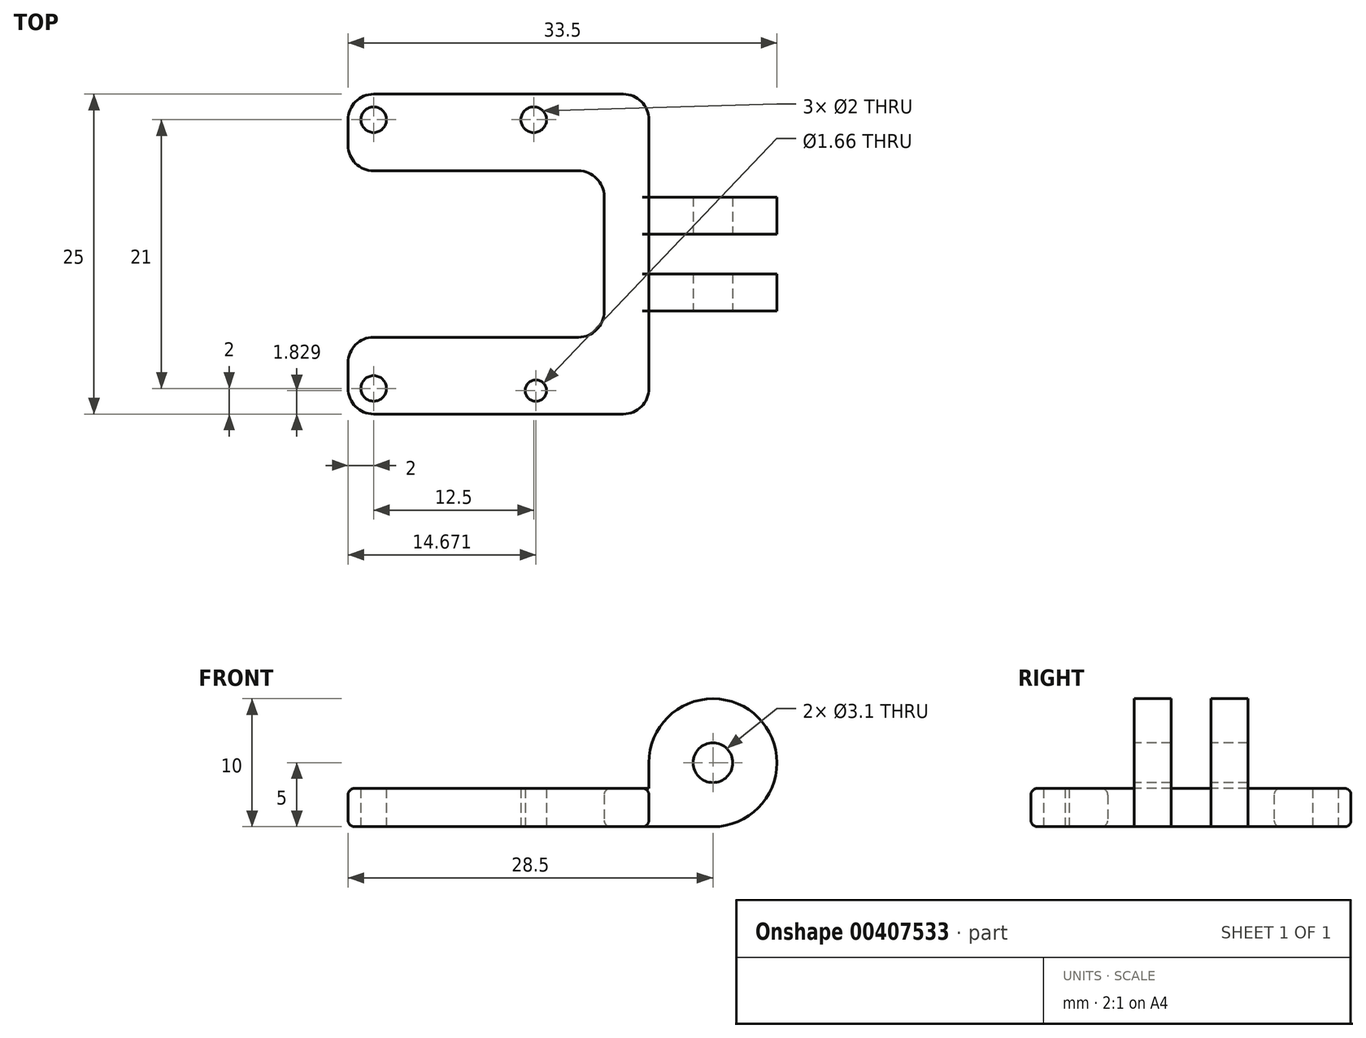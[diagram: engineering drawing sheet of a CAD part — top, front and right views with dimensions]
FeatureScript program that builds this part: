
annotation { "Feature Type Name" : "Feature", "Feature Type Description" : "" }
export const myFeature = defineFeature(function(context is Context, id is Id, definition is map)
    precondition{}
    {
        {
            var Q0;
            Q0=qCreatedBy(makeId("Top.planeOp"),FACE);
            var sketch = newSketch(context, id + "F0", { "sketchPlane" : qUnion([Q0])});
            skLineSegment(sketch, "E0.bottom", {"start": v(9.75, 12.5) * mm, "end": v(-9.75, 12.5) * mm});
            skLineSegment(sketch, "E0.top", {"start": v(9.75, -12.5) * mm, "end": v(-9.75, -12.5) * mm});
            skLineSegment(sketch, "E0.left", {"start": v(11.75, 10.5) * mm, "end": v(11.75, -1.55) * mm});
            skLineSegment(sketch, "E0.right", {"start": v(-11.75, 10.5) * mm, "end": v(-11.75, 8.5) * mm});
            skCircle(sketch, "E1", {"center": v(-9.75, -10.5) * mm, "radius": 1 * mm});
            skCircle(sketch, "E2", {"center": v(-9.75, 10.5) * mm, "radius": 1 * mm});
            skCircle(sketch, "E3", {"center": v(2.75, 10.5) * mm, "radius": 1 * mm});
            skCircle(sketch, "E4", {"center": v(2.92, -10.67) * mm, "radius": 0.83 * mm});
            skLineSegment(sketch, "E5.bottom", {"start": v(-9.75, 6.5) * mm, "end": v(6.25, 6.5) * mm});
            skLineSegment(sketch, "E5.top", {"start": v(-9.75, -6.5) * mm, "end": v(6.25, -6.5) * mm});
            skLineSegment(sketch, "E5.left", {"start": v(-11.75, 6.5) * mm, "end": v(-11.75, 6.5) * mm});
            skLineSegment(sketch, "E5.right", {"start": v(8.25, 4.5) * mm, "end": v(8.25, -4.5) * mm});
            skLineSegment(sketch, "E6", {"start": v(0, 0) * mm, "end": v(28.53, 0) * mm, "construction": true});
            skLineSegment(sketch, "E7", {"start": v(-11.75, -6.5) * mm, "end": v(-11.75, -6.5) * mm});
            skLineSegment(sketch, "E8", {"start": v(-11.75, -8.5) * mm, "end": v(-11.75, -10.5) * mm});
            skLineSegment(sketch, "E9", {"start": v(11.75, 4.45) * mm, "end": v(21.75, 4.45) * mm});
            skLineSegment(sketch, "E10", {"start": v(21.75, 4.45) * mm, "end": v(21.75, 1.55) * mm});
            skLineSegment(sketch, "E11", {"start": v(21.75, 1.55) * mm, "end": v(11.75, 1.55) * mm});
            skLineSegment(sketch, "E12", {"start": v(11.75, -1.55) * mm, "end": v(21.75, -1.55) * mm});
            skLineSegment(sketch, "E13", {"start": v(21.75, -1.55) * mm, "end": v(21.75, -4.45) * mm});
            skLineSegment(sketch, "E14", {"start": v(21.75, -4.45) * mm, "end": v(11.75, -4.45) * mm});
            skPoint(sketch, "E15.visualSharp", {"position": v(-11.75, 12.5) * mm});
            skArc(sketch, "E15.filletArc", {"start": v(-9.75, 12.5) * mm, "mid": v(-11.16, 11.91) * mm, "end": v(-11.75, 10.5) * mm});
            skPoint(sketch, "E16.visualSharp", {"position": v(-11.75, 6.5) * mm});
            skArc(sketch, "E16.filletArc", {"start": v(-11.75, 8.5) * mm, "mid": v(-11.16, 7.09) * mm, "end": v(-9.75, 6.5) * mm});
            skPoint(sketch, "E17.visualSharp", {"position": v(8.25, 6.5) * mm});
            skArc(sketch, "E17.filletArc", {"start": v(8.25, 4.5) * mm, "mid": v(7.66, 5.91) * mm, "end": v(6.25, 6.5) * mm});
            skPoint(sketch, "E18.visualSharp", {"position": v(8.25, -6.5) * mm});
            skArc(sketch, "E18.filletArc", {"start": v(6.25, -6.5) * mm, "mid": v(7.66, -5.91) * mm, "end": v(8.25, -4.5) * mm});
            skPoint(sketch, "E19.visualSharp", {"position": v(-11.75, -6.5) * mm});
            skArc(sketch, "E19.filletArc", {"start": v(-9.75, -6.5) * mm, "mid": v(-11.16, -7.09) * mm, "end": v(-11.75, -8.5) * mm});
            skPoint(sketch, "E20.visualSharp", {"position": v(-11.75, -12.5) * mm});
            skArc(sketch, "E20.filletArc", {"start": v(-11.75, -10.5) * mm, "mid": v(-11.16, -11.91) * mm, "end": v(-9.75, -12.5) * mm});
            skPoint(sketch, "E21.visualSharp", {"position": v(11.75, -12.5) * mm});
            skArc(sketch, "E21.filletArc", {"start": v(9.75, -12.5) * mm, "mid": v(11.16, -11.91) * mm, "end": v(11.75, -10.5) * mm});
            skPoint(sketch, "E22.visualSharp", {"position": v(11.75, 12.5) * mm});
            skArc(sketch, "E22.filletArc", {"start": v(11.75, 10.5) * mm, "mid": v(11.16, 11.91) * mm, "end": v(9.75, 12.5) * mm});
            skLineSegment(sketch, "E23", {"start": v(11.75, 1.55) * mm, "end": v(11.75, -4.45) * mm});
            skLineSegment(sketch, "E24", {"start": v(11.75, -4.45) * mm, "end": v(11.75, -10.5) * mm});
            skSolve(sketch);
        }
        {
            var Q0;
            Q0=makeQuery(id+"F0.imprint","IMPRINT",FACE,{"disambiguationData":[TD([[makeQuery(id+"F0.imprint","IMPRINT",EDGE,{"derivedFrom":sQuery(id+"F0.wireOp",EDGE,"E0.bottom")}),1.0]])]});
            extrude(context, id + "F1", {"entities" : qUnion([Q0]), "depth" : 3 * mm});
        }
        {
            var Q0;
            {var subQ2=sQuery(id+"F0.wireOp",EDGE,"E9");Q0=makeQuery(id+"F0.imprint","IMPRINT",FACE,{"disambiguationData":[TD([[makeQuery(id+"F0.imprint","IMPRINT",EDGE,{"derivedFrom":subQ2}),-1.0]])]});}
            var Q1;
            {var subQ0=sQuery(id+"F0.wireOp",EDGE,"E12");Q1=makeQuery(id+"F0.imprint","IMPRINT",FACE,{"disambiguationData":[TD([[makeQuery(id+"F0.imprint","IMPRINT",EDGE,{"derivedFrom":subQ0}),-1.0]])]});}
            extrude(context, id + "F2", {"entities" : qUnion([Q0, Q1]), "operationType" : NewBodyOperationType.ADD, "depth" : 10 * mm});
        }
        {
            var Q0;
            Q0=makeQuery(id+"F2.opExtrude","CAP_EDGE",EDGE,{"disambiguationData":[OSD([sQuery(id+"F0.wireOp",EDGE,"E23")])],"isStart":false});
            var Q1;
            Q1=makeQuery(id+"F2.opExtrude","CAP_EDGE",EDGE,{"disambiguationData":[OSD([sQuery(id+"F0.wireOp",EDGE,"E0.left")])],"isStart":false});
            var Q2;
            Q2=makeQuery(id+"F2.opExtrude","CAP_EDGE",EDGE,{"disambiguationData":[OSD([sQuery(id+"F0.wireOp",EDGE,"E10")])],"isStart":false});
            var Q3;
            Q3=makeQuery(id+"F2.opExtrude","CAP_EDGE",EDGE,{"disambiguationData":[OSD([sQuery(id+"F0.wireOp",EDGE,"E13")])],"isStart":false});
            var Q4;
            Q4=makeQuery(id+"F2.opExtrude","CAP_EDGE",EDGE,{"disambiguationData":[OSD([sQuery(id+"F0.wireOp",EDGE,"E10")])],"isStart":true});
            var Q5;
            Q5=makeQuery(id+"F2.opExtrude","CAP_EDGE",EDGE,{"disambiguationData":[OSD([sQuery(id+"F0.wireOp",EDGE,"E13")])],"isStart":true});
            fillet(context, id + "F3", {"entities" : qUnion([Q0, Q1, Q2, Q3, Q4, Q5]), "radius" : 5 * mm, "tangentPropagation" : true, "allowEdgeOverflow" : false});
        }
        {
            var Q0;
            Q0=makeQuery(id+"F2.opExtrude","SWEPT_FACE",FACE,{"disambiguationData":[OSD([sQuery(id+"F0.wireOp",EDGE,"E14")])]});
            var sketch = newSketch(context, id + "F4", { "sketchPlane" : qUnion([Q0])});
            skLineSegment(sketch, "E25", {"start": v(16.75, 0) * mm, "end": v(16.75, 10) * mm, "construction": true});
            skLineSegment(sketch, "E26", {"start": v(11.75, 5) * mm, "end": v(21.75, 5) * mm, "construction": true});
            skCircle(sketch, "E27", {"center": v(16.75, 5) * mm, "radius": 1.55 * mm});
            skSolve(sketch);
        }
        {
            var Q0;
            Q0=makeQuery(id+"F1.opExtrude","CAP_EDGE",EDGE,{"disambiguationData":[OSD([sQuery(id+"F0.wireOp",EDGE,"E5.bottom")])],"isStart":false});
            var Q1;
            {var subQ0=sQuery(id+"F0.wireOp",EDGE,"E0.left");var subQ1=sQuery(id+"F0.wireOp",EDGE,"E24");var subQ2=sQuery(id+"F0.wireOp",EDGE,"E23");var subQ3=makeQuery(id+"F1.opExtrude","SWEPT_FACE",FACE,{"disambiguationData":[OSD([subQ0,subQ2,subQ1])]});var subQ4=makeQuery(id+"F1.opExtrude","CAP_FACE",FACE,{"disambiguationData":[OSD([sQuery(id+"F0.wireOp",EDGE,"E0.bottom"),sQuery(id+"F0.wireOp",EDGE,"E0.top"),subQ0,sQuery(id+"F0.wireOp",EDGE,"E0.right"),sQuery(id+"F0.wireOp",EDGE,"E1"),sQuery(id+"F0.wireOp",EDGE,"E2"),sQuery(id+"F0.wireOp",EDGE,"E3"),sQuery(id+"F0.wireOp",EDGE,"E4"),sQuery(id+"F0.wireOp",EDGE,"E5.bottom"),sQuery(id+"F0.wireOp",EDGE,"E5.top"),sQuery(id+"F0.wireOp",EDGE,"E5.right"),sQuery(id+"F0.wireOp",EDGE,"E8"),sQuery(id+"F0.wireOp",EDGE,"E15.filletArc"),sQuery(id+"F0.wireOp",EDGE,"E16.filletArc"),sQuery(id+"F0.wireOp",EDGE,"E17.filletArc"),sQuery(id+"F0.wireOp",EDGE,"E18.filletArc"),sQuery(id+"F0.wireOp",EDGE,"E19.filletArc"),sQuery(id+"F0.wireOp",EDGE,"E20.filletArc"),sQuery(id+"F0.wireOp",EDGE,"E21.filletArc"),sQuery(id+"F0.wireOp",EDGE,"E22.filletArc"),subQ2,subQ1])],"isStart":false});Q1=makeQuery(id+"F2.boolean.opBoolean","SPLIT",EDGE,{"disambiguationData":[topologyDisambiguationEdgeConnected([subQ4,subQ3]),TD([makeQuery(id+"F2.opExtrude","SWEPT_FACE",FACE,{"disambiguationData":[OSD([sQuery(id+"F0.wireOp",EDGE,"E11")])]})])],"derivedFrom":makeQuery(id+"F1.opExtrude","CAP_EDGE",EDGE,{"disambiguationData":[OSD([subQ0,subQ2,subQ1])],"isStart":false})});}
            var Q2;
            Q2=makeQuery(id+"F1.opExtrude","CAP_EDGE",EDGE,{"disambiguationData":[OSD([sQuery(id+"F0.wireOp",EDGE,"E0.top")])],"isStart":true});
            var Q3;
            {var subQ0=sQuery(id+"F0.wireOp",EDGE,"E11");var subQ1=sQuery(id+"F0.wireOp",EDGE,"E0.left");var subQ2=sQuery(id+"F0.wireOp",EDGE,"E24");var subQ3=sQuery(id+"F0.wireOp",EDGE,"E23");Q3=makeQuery(id+"F2.boolean.opBoolean","SPLIT",EDGE,{"disambiguationData":[TD([makeQuery(id+"F2.opExtrude","SWEPT_FACE",FACE,{"disambiguationData":[OSD([subQ0])]})])],"derivedFrom":makeQuery(id+"F1.opExtrude","CAP_EDGE",EDGE,{"disambiguationData":[OSD([subQ1,subQ3,subQ2])],"isStart":true})});}
            fillet(context, id + "F5", {"entities" : qUnion([Q0, Q1, Q2, Q3]), "radius" : 0.5 * mm, "tangentPropagation" : true, "allowEdgeOverflow" : false});
        }
        {
            var Q0;
            Q0=makeQuery(id+"F4.imprint","IMPRINT",FACE,{"disambiguationData":[TD([[makeQuery(id+"F4.imprint","IMPRINT",EDGE,{"derivedFrom":sQuery(id+"F4.wireOp",EDGE,"E27")}),1.0]])]});
            extrude(context, id + "F6", {"entities" : qUnion([Q0]), "operationType" : NewBodyOperationType.REMOVE, "oppositeDirection" : true, "depth" : 8.9 * mm});
        }
    });
